# Revit family: 2015_Ventana_Alugom_65-Optima_Balconera-Monoblock-1-Hoja_JGJGJG
name_source: partatom
category: Ventanas
revit_build: Autodesk Revit 2015 (Build: 20140606_1530(x64)
units: mm (PartAtom-declared; Revit-internal decimal feet)

## types (1)
- 800 x 2000 mm Balconera
    AcidificacionAtmosferica = 0
    AcidificacionAtmosfericaPorUnidad = 0
    Acristalamiento = Cristal - Vidrio claro templado
    AguaConsumida = 0
    AguaConsumidaPorUnidad = 0
    Altura = 2000 mm  [stored 6.56168 ft]
    Altura Máxima = 2500 mm  [stored 8.2021 ft]
    Altura Real = 2000 mm  [stored 6.56168 ft]
    Altura de antepecho por defecto = 0 mm  [stored 0 ft]
    AnchoMarco = 143 mm
    AnchoMarcoCentral = 195 mm  [stored 0.639764 ft]
    Anchura = 800 mm  [stored 2.62467 ft]
    Anchura Máxima = 1700 mm  [stored 5.57743 ft]
    Anchura Real = 800 mm  [stored 2.62467 ft]
    Area = 1600000 mm²
    Autor = Bimetica Parametric Design Services, S.L.
    Bimetica = http://www.bimetica.com
    CambioClimatico = 0
    CambioClimaticoPorUnidad = 0
    CerramientoExterior = Sí
    Cierre de muro = Por anfitrión
    Comentarios de tipo = Sistema de Ventana Balconera con Monoblock de 1 Hoja Rotura de Puente Térmico Serie 65 Óptima Practicable.
    ConfiguracionPoliamidas = 320300 - 464700 - 464600 - 479900
    ControlHumos = Sí
    CosteEnergeticoKwh = 0
    CosteEnergeticoMj = 0 J
    CosteMantenimiento = 0
    Descripción = Balconera Monoblock
    DesfaseExterior = 0 mm  [stored 0 ft]
    DesfaseInterior = 0 mm  [stored 0 ft]
    DestruccionCapaOzonoEstratosferica = 0
    DestruccionCapaOzonoEstratosfericaPorUnidad = 0
    Detalle Perfileria = Sí
    EmisionCO2 = 0
    EnergiaNoRenovableConsumida = 0
    EnergiaNoRenovableConsumidaPorUnidad = 0
    EnergiaPrimariaTotalConsumida = 0
    EnergiaPrimariaTotalConsumidaPorUnidad = 0
    EnergiaRenovableConsumida = 0
    EnergiaRenovableConsumidaPorUnidad = 0
    EstanqueidadAgua = Clase E3300
    Eutrofizacion = 0
    EutrofizacionPorUnidad = 0
    Fabricante = Grupo ALUGOM
    FactorSolarModificado = 3000000
    FactorSombra = 0
    FaltaDeRecursos = 0
    FaltaDeRecursosPorUnidad = 0
    FechaEmisionElementoBIM = 02/09/2016
    FechaVencimientoElementoBIM = 02/09/2017
    FormacionFotoquimicaOzono = 0
    FormacionFotoquimicaOzonoPorUnidad = 0
    FraccionAreaAcristalamiento = 0.00%
    GrosorAcristalamiento = 39 mm  [stored 0.127953 ft]
    GrosorMarco = 65 mm  [stored 0.213255 ft]
    IndiceGlobalRedAcustica = 47dBA
    InformacionTecnica = http://www.alugom.com
    Manija = Sí
    Marco = Aluminio
    MasaSuperficialKgm2 = 0
    MasterformatCodigo = 08 51 13
    MasterformatTitulo = Aluminium Windows
    MateriaPrima = 0
    Modelo = Serie 65 Óptima
    Motorizada = No
    OmniclassCodigo = 23.30.20.17.21.21
    OmniclassTitulo = Casment Window
    Operación = Practicable
    Oscilobatiente = No
    Perimetro = 5600
    PermeabilidadAlAire = Clase 4
    Poliamida = Poliamida, Technoform Bautec, PA66 GF 25
    Practicable = Sí
    ReferenciaContacto = Alugom
    RepisaExterior = No
    RepisaInterior = No
    ResiduoInerte = 0
    ResiduoInertePorUnidad = 0
    ResiduoRadioactivo = 0
    ResiduoRadioactivoPorUnidad = 0
    ResiduosNoPeligrosos = 0
    ResiduosNoPeligrososPorUnidad = 0
    ResiduosPeligrosos = 0
    ResiduosPeligrososPorUnidad = 0
    ResistenciaAlViento = Clase 5
    SalidaEmergencia = Sí
    TelefonoContacto = +34 91 616 47 27
    TransmitanciaTermica = 0 W/(m²·K)
    UNSPSCCodigo = 30171600
    UNSPSCTitulo = Windows
    URL = http://www.alugom.com
    URL Poliamida = http://www.technoform.es
    URL Poliamida - Catálogo = http://www.technoform.com
    URLProducto = http://www.alugom.com
    Uniclass2.0Codigo = "25-30"
    Uniclass2.0Titulo = "Door and window systems"
    VersionElementoBIM = 1.0
    Y𝑔 = 0.11
    𝐴𝑓 = 716775
    𝐴𝑔 = 883225
    𝑈𝑓 = 3.629
    𝑈𝑔 = 1.9
    𝑈𝑤 = 2.98119
    𝑙𝑔 = 4460

note: [stored X ft] marks values corroborated as IEEE doubles in the binary element streams (Revit-internal decimal feet)
